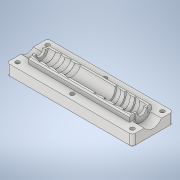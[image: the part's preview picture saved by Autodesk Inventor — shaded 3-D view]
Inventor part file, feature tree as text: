
AUTODESK INVENTOR PART (.ipt)
format: ipt  version: 2020.2 (Build 242310000, 310)  size: 503,808 bytes
history: native  units: mm
features: sketch x13, extrude x12, projected_geometry x9, fillet x2, other x1, mirror x1, boolean_combine x1, chamfer x1
ambient origin geometry x8: Origin, YZ Plane, XZ Plane, XY Plane, X Axis, Y Axis, Z Axis, Center Point
bodies: Volumenkörper1 (feature_tree), Solid2 (feature_tree), Solid3 (feature_tree)
feature tree (40):
  extrude  "Extrusion1"  Depth=6.0mm
  other  "Spirale1"
  mirror  "Spiegeln1"
  extrude  "Extrusion5"  Depth=4.0mm
  extrude  "Extrusion6"  Depth=1.0mm
  boolean_combine  "Combine1"
  extrude  "Extrusion7"  Depth=10.0mm TaperAngle=0.0deg
  extrude  "Extrusion8"  Depth=100.0mm TaperAngle=0.0deg
  extrude  "Extrusion9"  Depth=24.0mm
  extrude  "Extrusion10"  Depth=12.0mm TaperAngle=0.0deg
  extrude  "Extrusion11"  Depth=16.0mm
  chamfer  "Chamfer2"  Distance=4.0mm
  extrude  "Extrusion12"  Depth=3.0mm
  fillet  "Fillet1"  Radius=3.0mm
  extrude  "Extrusion13"  Depth=4.0mm
  fillet  "Fillet2"  Radius=4.0mm
  extrude  "Extrusion14"  Depth=4.0mm
  extrude  "Extrusion15"  Depth=4.0mm
  sketch  "Skizze1"  dims[d0=6.0mm d1=11.0mm]
  sketch  "Skizze3"  dims[d2=36.0mm d3=0.0mm]
  projected_geometry  "Projizierte Kontur2"
  sketch  "Sketch7"  dims[d8=7.0mm d9=24.5mm d10=10.0mm d11=0.0mm d12=90.0deg d13=90.0deg d14=0.0mm d15=0.0mm d16=4.0mm]
  sketch  "Sketch8"  dims[d17=13.962634mm d18=1.0mm]
  sketch  "Sketch9"  dims[d19=0.1mm d32=10.0mm d33=0.0mm]
  projected_geometry  "Projected Loop4"
  sketch  "Sketch10"  dims[d34=7.0mm d35=100.0mm d36=0.0mm]
  projected_geometry  "Projected Loop5"
  projected_geometry  "Projected Loop6"
  projected_geometry  "Projected Loop7"
  projected_geometry  "Projected Loop8"
  sketch  "Sketch11"  dims[d37=82.0mm d38=0.0mm d39=24.0mm]
  projected_geometry  "Projected Loop9"
  sketch  "Sketch12"  dims[d40=30.0mm d41=12.0mm d42=0.0mm]
  sketch  "Sketch13"  dims[d43=74.0mm d44=16.0mm]
  projected_geometry  "Projected Loop10"
  projected_geometry  "Projected Loop11"
  sketch  "Sketch14"  dims[d45=79.0mm]
  sketch  "Sketch15"  dims[d46=21.0mm d47=4.0mm d48=0.0mm]
  sketch  "Sketch16"  dims[d49=3.0mm d50=3.0mm d51=3.0mm]
  sketch  "Sketch17"  dims[d52=3.0mm d53=4.0mm d54=4.0mm d55=4.0mm d56=4.0mm d57=4.0mm d58=4.0mm d59=4.0mm d60=4.0mm d61=10.0mm d62=0.0mm d63=1.0mm d64=1.0mm d65=1.0mm d66=1.0mm d67=6.0mm d68=10.0mm d69=0.0mm d70=10.0mm d71=0.0mm d72=1.0mm d73=2.0mm d74=45.0deg d75=3.0mm d76=3.0mm d77=4.0mm d78=46.0mm d79=4.0mm d80=44.0mm d81=5.5mm d82=5.5mm d83=5.5mm d84=5.5mm d85=5.5mm d86=5.5mm d87=5.0mm d88=0.0mm d89=2.0mm d90=0.5mm d91=6.5mm d92=74.1mm d93=2.1mm d94=0.0mm d95=0.0mm d96=1.0mm d97=12.0mm d98=0.2mm d99=7.9mm d100=0.0mm d101=0.0mm d102=15.0mm d103=0.2mm d104=7.9mm d105=0.0mm d106=0.0mm]
